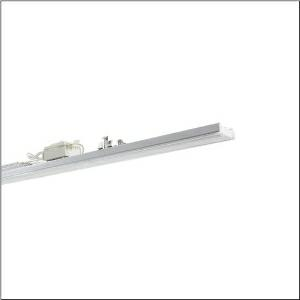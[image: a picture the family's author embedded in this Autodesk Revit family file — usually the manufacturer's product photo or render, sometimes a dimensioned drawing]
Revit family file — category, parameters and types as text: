
# Revit family: licross_21_recessed_ho_52tl1wdn4fxm
name_source: partatom
category: Lighting Fixtures
units: mm (PartAtom-declared; Revit-internal decimal feet)

## family parameters
Cut with Voids When Loaded = No
Host = Face
Light Source = No
Part Type = Normal
Room Calculation Point = No
Round Connector Dimension = Use Diameter
Shared = No

## types (1)
- --- (1 x LED, 15050 lm, 84.6 W, 4000K)
    Apparent Load = 85 VA
    CIE Flux Codes = 73 94 99 100 100
    Color Rendering = 80
    Color Temperature = 4000K
    Default Elevation = 1800 mm
    Description = Licross 21 Recessed HO, luminaire insert, of sheet steel, galvanised, coil coated, white, length: 1.500mm, width: 66mm, height: 67mm, LED rated luminous flux: 15.050lm, light colour: 840, SDCM (Standard Deviation of Colour Matching)MacAdam ≤ 3 SDCM (initial), control gear: DALI 2, with plug, 5-pole, with phase selection, mains connection: 220..240V, AC, 50/60Hz, rated input power: 85W, internal wiring halogen-free, primary optical cover: cover, of PMMA, light emission: direct distribution, primary light characteristic: symmetric, protection rating (complete): IP40, insulation class (complete): insulation class I (protective earthing), certification: CE, ENEC, VDE, UKCA, protection symbol: D if used in an environment without relevant dust loads with corresponding accessories, impact resistance: IK06, permissible ambient temperature for indoor applications: -25..+30°C, corresponds to IFS (International Featured Standards) requirements for safety and quality in the food industry, reducing of maximum allowable ambient temperature of 5°C with ceiling mounting, LABS conformity tested according to VDMA 24364:2018-05, The light source and the operating device comply with the requirements of the Ecodesign Regulation (EU) 2019/2020 and are replaceable in accordance with this regulation, packaging unit: 1 piece
    Height = 58 mm
    Lamp = 1 x LED
    Lamp Light Flux = 15050 lm
    Lamp Power = 84.6 W
    Lamp count = 1
    Length = 1500 mm
    Luminous efficacy = 178 lm/W
    Manufacturer = Siteco
    ModVariant = No
    Model = 52TL1WDN4FXM
    Mounting Place = Ceiling
    Mounting Type = Pendant
    Number of Poles = 1
    OnlyDefault = Yes
    Power Factor = 1
    Product Name = Licross 21 Recessed HO
    Product group = luminaire insert | ceiling pendant
    ProductGroupID = 901
    Protection Class = Protection class I
    Protection Degree = IP 40
    RLX_Detail_Level = 1
    RLX_Emergency_Light_Flux = 0 lm
    RLX_Emergency_Type = 0
    RLX_Emergency_Type_DB = No
    RlxData = <blob elided: 24877 chars, md5=d0d64a11>
    Socket = socket
    Standby Power = 0 W
    System Light Flux = 15050 lm
    System Power = 85 W
    Type Comments = factory setting: luminous flux: 100 % | dim-lin: 254 | 484 mA
    Type Image = l_1296930.jpg
    URL = http://relux.com
    VarID = @adj_066669
    Voltage = 0 V
    Weight = 0.00 kg
    Width = 66 mm

## geometry (parser evidence)
native form markers: Blend x4, Sweep x12
no freeform markers — native parametric forms only
